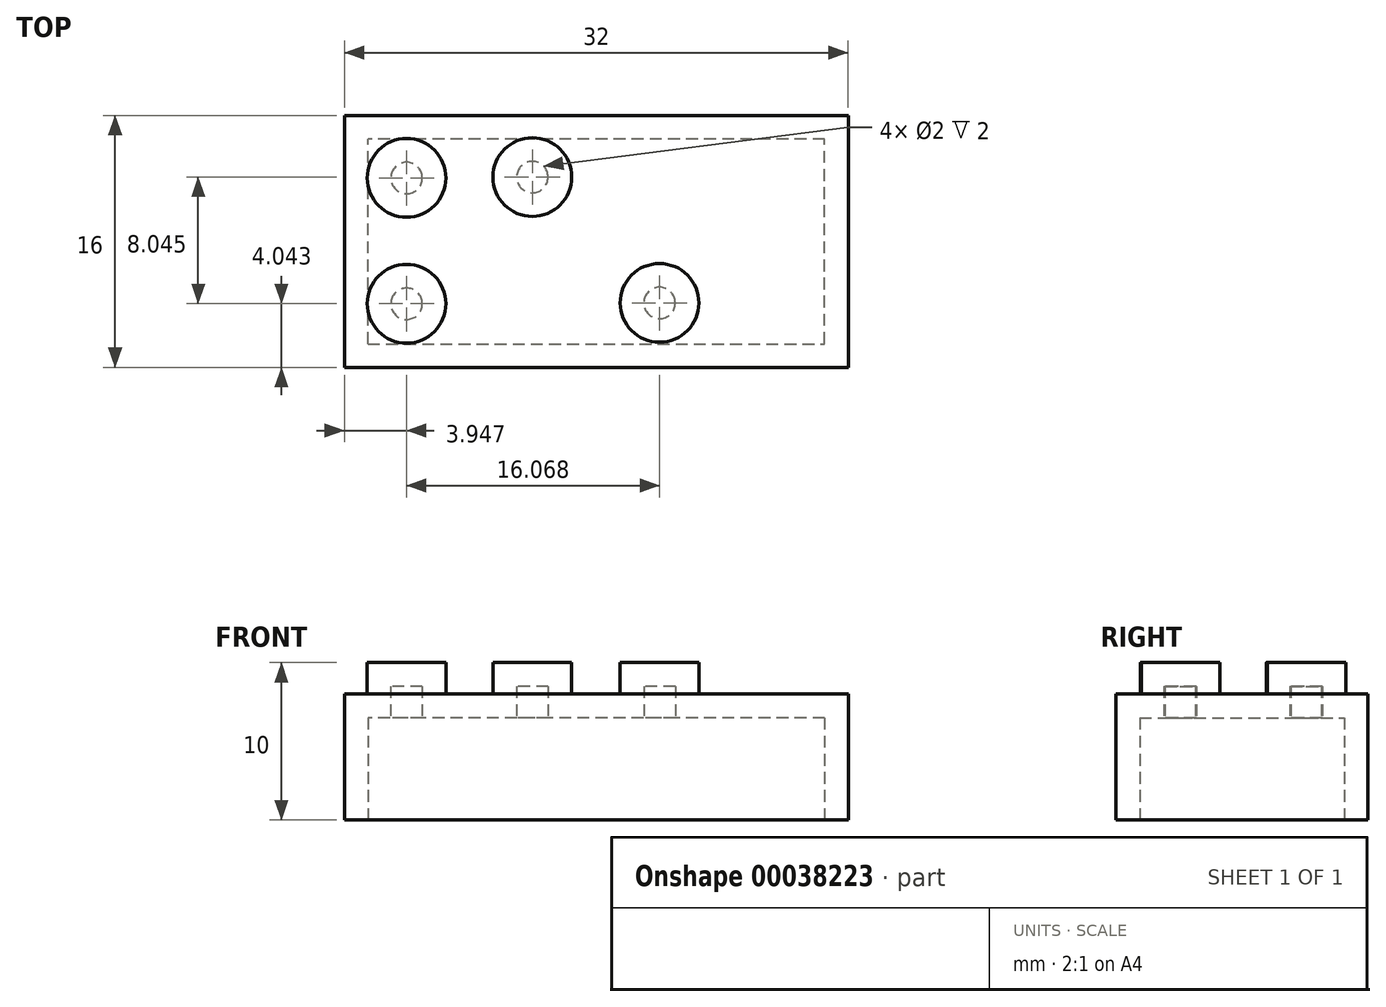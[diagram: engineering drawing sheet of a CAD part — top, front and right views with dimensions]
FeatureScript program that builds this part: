
annotation { "Feature Type Name" : "Feature", "Feature Type Description" : "" }
export const myFeature = defineFeature(function(context is Context, id is Id, definition is map)
    precondition{}
    {
        {
            var Q0;
            Q0=qCreatedBy(makeId("Top.planeOp"),FACE);
            var sketch = newSketch(context, id + "F0", { "sketchPlane" : qUnion([Q0])});
            skLineSegment(sketch, "E0", {"start": v(-14.12, 0) * mm, "end": v(17.88, 0) * mm});
            skLineSegment(sketch, "E1", {"start": v(17.88, 0) * mm, "end": v(17.88, 16) * mm});
            skLineSegment(sketch, "E2", {"start": v(-14.12, 0) * mm, "end": v(-14.12, 16) * mm});
            skLineSegment(sketch, "E3", {"start": v(17.88, 16) * mm, "end": v(-14.12, 16) * mm});
            skLineSegment(sketch, "E4", {"start": v(-14.12, 0) * mm, "end": v(1.88, 0) * mm});
            skLineSegment(sketch, "E5.left", {"start": v(-14.12, 8) * mm, "end": v(-14.12, 8.06) * mm});
            skLineSegment(sketch, "E6", {"start": v(17.88, 0) * mm, "end": v(9.17, 0) * mm});
            skLineSegment(sketch, "E7", {"start": v(9.17, 0) * mm, "end": v(8.38, 0) * mm});
            skArc(sketch, "E8.MirrorC", {"start": v(17.88, 8.29) * mm, "mid": v(17.9, 8.06) * mm, "end": v(17.88, 7.82) * mm});
            skSolve(sketch);
        }
        {
            var Q0;
            Q0=makeQuery(id+"F0.imprint","IMPRINT",FACE,{"disambiguationData":[TD([[makeQuery(id+"F0.imprint","IMPRINT",EDGE,{"derivedFrom":sQuery(id+"F0.wireOp",EDGE,"E0")}),1.0]])]});
            extrude(context, id + "F1", {"entities" : qUnion([Q0]), "depth" : 8 * mm});
        }
        {
            var Q0;
            Q0=qCreatedBy(makeId("Top.planeOp"),FACE);
            cPlane(context, id + "F2", {"entities" : qUnion([Q0]), "cplaneType" : CPlaneType.OFFSET, "offset" : 8 * mm, "width" : 150 * mm, "height" : 150 * mm});
        }
        {
            var Q0;
            Q0=qCreatedBy(id+"F2.planeOp",FACE);
            var sketch = newSketch(context, id + "F3", { "sketchPlane" : qUnion([Q0])});
            skLineSegment(sketch, "E9", {"start": v(-15.62, 16) * mm, "end": v(-15.62, 16.08) * mm});
            skCircle(sketch, "E10", {"center": v(-10.17, 12.04) * mm, "radius": 2.5 * mm});
            skLineSegment(sketch, "E11.right", {"start": v(-2.18, 14.82) * mm, "end": v(-2.18, 14.59) * mm});
            skCircle(sketch, "E12", {"center": v(-2.18, 12.09) * mm, "radius": 2.5 * mm});
            skLineSegment(sketch, "E13.trimOffspring", {"start": v(-2.18, 14.82) * mm, "end": v(-2.17, 14.82) * mm});
            skCircle(sketch, "E14", {"center": v(-10.17, 4.04) * mm, "radius": 2.5 * mm});
            skCircle(sketch, "E15", {"center": v(-2.18, 4.1) * mm, "radius": 2.5 * mm});
            skPoint(sketch, "E16.left.start.orphan", {"position": v(-14.14, 12.04) * mm});
            skPoint(sketch, "E17.end.orphan", {"position": v(10.93, 0) * mm});
            skCircle(sketch, "E18.MirrorC", {"center": v(5.9, 12.09) * mm, "radius": 2.5 * mm});
            skCircle(sketch, "E19.MirrorC", {"center": v(13.89, 12.04) * mm, "radius": 2.5 * mm});
            skCircle(sketch, "E20.MirrorC", {"center": v(13.89, 4.04) * mm, "radius": 2.5 * mm});
            skCircle(sketch, "E21.MirrorC", {"center": v(5.9, 4.1) * mm, "radius": 2.5 * mm});
            skPoint(sketch, "E22.end.orphan", {"position": v(1.86, 0) * mm});
            skSolve(sketch);
        }
        {
            var Q0;
            Q0=makeQuery(id+"F3.imprint","IMPRINT",FACE,{"disambiguationData":[TD([[makeQuery(id+"F3.imprint","IMPRINT",EDGE,{"derivedFrom":sQuery(id+"F3.wireOp",EDGE,"E10")}),1.0]])]});
            var Q1;
            Q1=makeQuery(id+"F3.imprint","IMPRINT",FACE,{"disambiguationData":[TD([[makeQuery(id+"F3.imprint","IMPRINT",EDGE,{"derivedFrom":sQuery(id+"F3.wireOp",EDGE,"E14")}),1.0]])]});
            var Q2;
            Q2=makeQuery(id+"F3.imprint","IMPRINT",FACE,{"disambiguationData":[TD([[makeQuery(id+"F3.imprint","IMPRINT",EDGE,{"derivedFrom":sQuery(id+"F3.wireOp",EDGE,"E15")}),-1.0]])]});
            var Q3;
            Q3=makeQuery(id+"F3.imprint","IMPRINT",FACE,{"disambiguationData":[TD([[makeQuery(id+"F3.imprint","IMPRINT",EDGE,{"derivedFrom":sQuery(id+"F3.wireOp",EDGE,"E12")}),1.0]])]});
            var Q4;
            Q4=makeQuery(id+"F3.imprint","IMPRINT",FACE,{"disambiguationData":[TD([[makeQuery(id+"F3.imprint","IMPRINT",EDGE,{"derivedFrom":sQuery(id+"F3.wireOp",EDGE,"E18.MirrorC")}),-1.0]])]});
            var Q5;
            Q5=makeQuery(id+"F3.imprint","IMPRINT",FACE,{"disambiguationData":[TD([[makeQuery(id+"F3.imprint","IMPRINT",EDGE,{"derivedFrom":sQuery(id+"F3.wireOp",EDGE,"E21.MirrorC")}),1.0]])]});
            var Q6;
            Q6=makeQuery(id+"F3.imprint","IMPRINT",FACE,{"disambiguationData":[TD([[makeQuery(id+"F3.imprint","IMPRINT",EDGE,{"derivedFrom":sQuery(id+"F3.wireOp",EDGE,"E20.MirrorC")}),-1.0]])]});
            var Q7;
            Q7=makeQuery(id+"F3.imprint","IMPRINT",FACE,{"disambiguationData":[TD([[makeQuery(id+"F3.imprint","IMPRINT",EDGE,{"derivedFrom":sQuery(id+"F3.wireOp",EDGE,"E19.MirrorC")}),-1.0]])]});
            extrude(context, id + "F4", {"entities" : qUnion([Q0, Q1, Q2, Q3, Q4, Q5, Q6, Q7]), "operationType" : NewBodyOperationType.ADD, "depth" : 2 * mm});
        }
        {
            var Q0;
            Q0=makeQuery(id+"F1.opExtrude","CAP_FACE",FACE,{"disambiguationData":[OSD([sQuery(id+"F0.wireOp",EDGE,"E0"),sQuery(id+"F0.wireOp",EDGE,"E1"),sQuery(id+"F0.wireOp",EDGE,"E2"),sQuery(id+"F0.wireOp",EDGE,"E3")])],"isStart":true});
            shell(context, id + "F5", {"entities" : qUnion([Q0]), "thickness" : 1.5 * mm});
        }
    });
